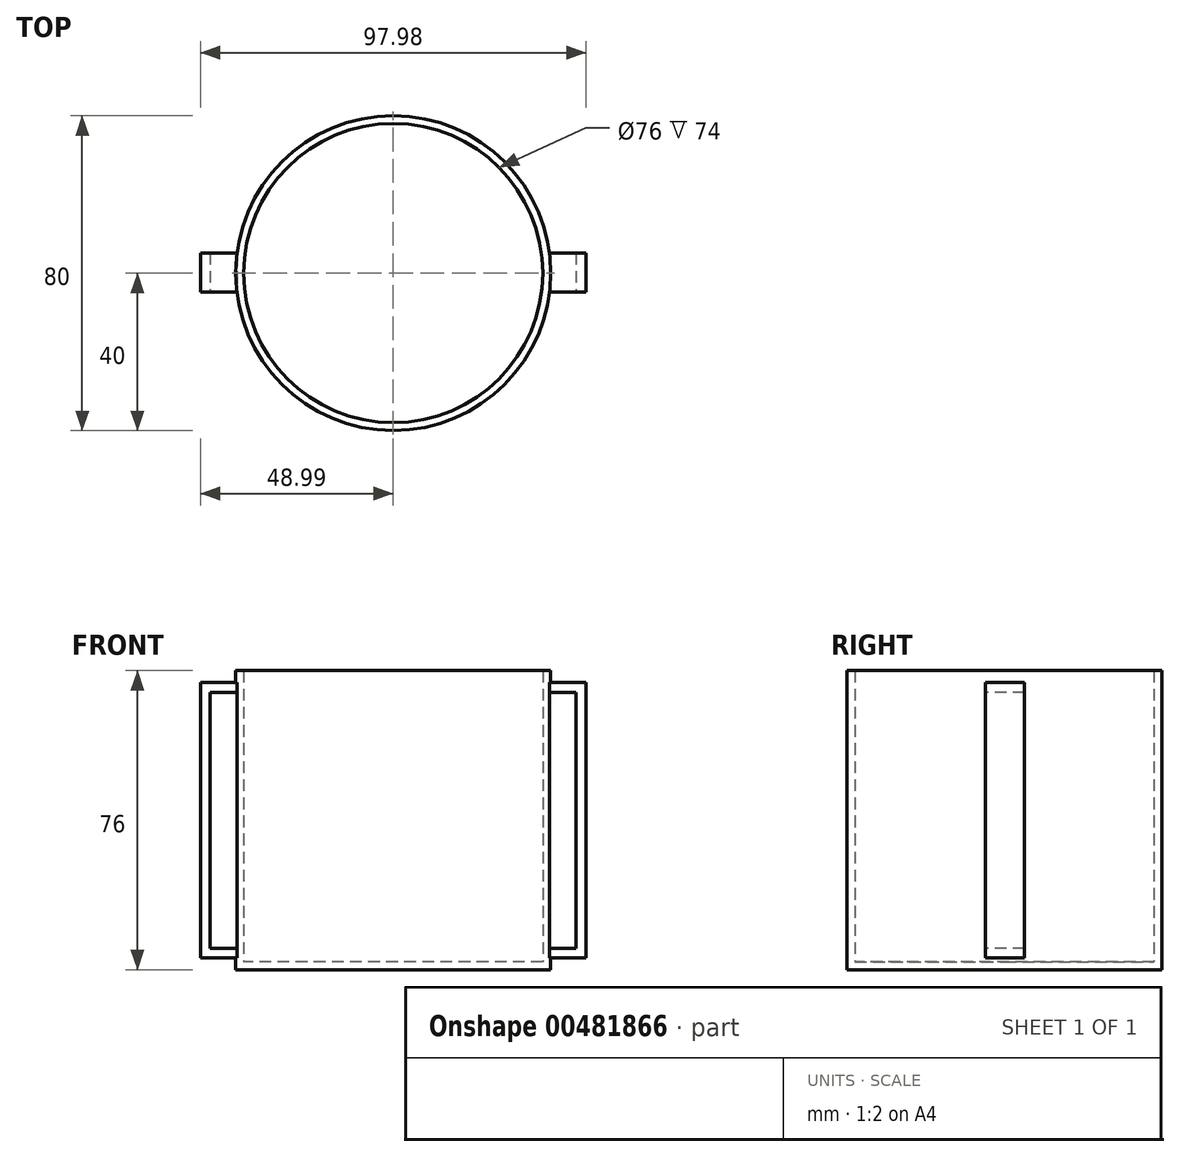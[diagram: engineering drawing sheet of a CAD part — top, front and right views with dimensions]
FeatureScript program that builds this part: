
annotation { "Feature Type Name" : "Feature", "Feature Type Description" : "" }
export const myFeature = defineFeature(function(context is Context, id is Id, definition is map)
    precondition{}
    {
        {
            var Q0;
            Q0=qCreatedBy(makeId("Top.planeOp"),FACE);
            var sketch = newSketch(context, id + "F0", { "sketchPlane" : qUnion([Q0])});
            skCircle(sketch, "E0", {"center": v(0, 0) * mm, "radius": 40 * mm});
            skLineSegment(sketch, "E1", {"start": v(-3, 39.89) * mm, "end": v(-3, 43.89) * mm});
            skLineSegment(sketch, "E2", {"start": v(-3, 43.89) * mm, "end": v(3, 43.89) * mm});
            skLineSegment(sketch, "E3", {"start": v(3, 43.89) * mm, "end": v(3, 39.89) * mm});
            skSolve(sketch);
        }
        {
            var Q0;
            {var subQ0=sQuery(id+"F0.wireOp",EDGE,"E0");var subQ1=makeQuery(id+"F0.imprint","INTERSECT",VERTEX,{"derivedFrom":[subQ0,sQuery(id+"F0.wireOp",EDGE,"E1")]});Q0=makeQuery(id+"F0.imprint","IMPRINT",FACE,{"disambiguationData":[TD([[makeQuery(id+"F0.imprint","IMPRINT",EDGE,{"disambiguationData":[TD([[subQ1,1.0]])],"derivedFrom":subQ0}),1.0]])]});}
            extrude(context, id + "F1", {"entities" : qUnion([Q0]), "endBound" : BoundingType.SYMMETRIC, "depth" : 76 * mm});
        }
        {
            var Q0;
            Q0=makeQuery(id+"F1.opExtrude","CAP_FACE",FACE,{"disambiguationData":[OSD([sQuery(id+"F0.wireOp",EDGE,"E0")])],"isStart":false});
            shell(context, id + "F2", {"entities" : qUnion([Q0]), "thickness" : 2 * mm});
        }
        {
            var Q0;
            Q0=qCreatedBy(makeId("Top.planeOp"),FACE);
            var sketch = newSketch(context, id + "F3", { "sketchPlane" : qUnion([Q0])});
            skLineSegment(sketch, "E4.bottom", {"start": v(-49, 5.15) * mm, "end": v(-39, 5.15) * mm});
            skLineSegment(sketch, "E4.top", {"start": v(-49, -4.85) * mm, "end": v(-39, -4.85) * mm});
            skLineSegment(sketch, "E4.left", {"start": v(-49, 5.15) * mm, "end": v(-49, -4.85) * mm});
            skLineSegment(sketch, "E4.right", {"start": v(-39, 5.15) * mm, "end": v(-39, -4.85) * mm});
            skLineSegment(sketch, "E5.MirrorCS", {"start": v(49, 5.15) * mm, "end": v(39, 5.15) * mm});
            skLineSegment(sketch, "E6.MirrorCS", {"start": v(49, -4.85) * mm, "end": v(39, -4.85) * mm});
            skLineSegment(sketch, "E7.MirrorCS", {"start": v(49, 5.15) * mm, "end": v(49, -4.85) * mm});
            skLineSegment(sketch, "E8.MirrorCS", {"start": v(39, 5.15) * mm, "end": v(39, -4.85) * mm});
            skSolve(sketch);
        }
        {
            var Q0;
            Q0 = qSketchRegion(id + "F3", true);
            extrude(context, id + "F4", {"entities" : qUnion([Q0]), "operationType" : NewBodyOperationType.ADD, "endBound" : BoundingType.SYMMETRIC, "depth" : 70 * mm, "offsetDistance" : 25 * mm});
        }
        {
            var Q0;
            Q0=makeQuery(id+"F4.opExtrude","SWEPT_FACE",FACE,{"disambiguationData":[OSD([sQuery(id+"F3.wireOp",EDGE,"E4.top")])]});
            var sketch = newSketch(context, id + "F5", { "sketchPlane" : qUnion([Q0])});
            skLineSegment(sketch, "E9.bottom", {"start": v(-46.5, 32.5) * mm, "end": v(-39.7, 32.5) * mm});
            skLineSegment(sketch, "E9.top", {"start": v(-46.5, -32.5) * mm, "end": v(-39.7, -32.5) * mm});
            skLineSegment(sketch, "E9.left", {"start": v(-46.5, 32.5) * mm, "end": v(-46.5, -32.5) * mm});
            skLineSegment(sketch, "E9.right", {"start": v(-39.7, 32.5) * mm, "end": v(-39.7, -32.5) * mm});
            skSolve(sketch);
        }
        {
            var Q0;
            Q0=makeQuery(id+"F5.imprint","IMPRINT",FACE,{"disambiguationData":[TD([[makeQuery(id+"F5.imprint","IMPRINT",EDGE,{"derivedFrom":sQuery(id+"F5.wireOp",EDGE,"E9.bottom")}),-1.0]])]});
            extrude(context, id + "F6", {"entities" : qUnion([Q0]), "operationType" : NewBodyOperationType.REMOVE, "oppositeDirection" : true, "depth" : 25 * mm, "offsetDistance" : 25 * mm});
        }
        {
            var Q0;
            Q0=makeQuery(id+"F4.opExtrude","SWEPT_FACE",FACE,{"disambiguationData":[OSD([sQuery(id+"F3.wireOp",EDGE,"E6.MirrorCS")])]});
            var sketch = newSketch(context, id + "F7", { "sketchPlane" : qUnion([Q0])});
            skLineSegment(sketch, "E10.bottom", {"start": v(39.7, 32.5) * mm, "end": v(46.5, 32.5) * mm});
            skLineSegment(sketch, "E10.top", {"start": v(39.7, -32.5) * mm, "end": v(46.5, -32.5) * mm});
            skLineSegment(sketch, "E10.left", {"start": v(39.7, 32.5) * mm, "end": v(39.7, -32.5) * mm});
            skLineSegment(sketch, "E10.right", {"start": v(46.5, 32.5) * mm, "end": v(46.5, -32.5) * mm});
            skSolve(sketch);
        }
        {
            var Q0;
            Q0=makeQuery(id+"F7.imprint","IMPRINT",FACE,{"disambiguationData":[TD([[makeQuery(id+"F7.imprint","IMPRINT",EDGE,{"derivedFrom":sQuery(id+"F7.wireOp",EDGE,"E10.bottom")}),-1.0]])]});
            extrude(context, id + "F8", {"entities" : qUnion([Q0]), "operationType" : NewBodyOperationType.REMOVE, "oppositeDirection" : true, "depth" : 25 * mm, "offsetDistance" : 25 * mm});
        }
    });
